# Revit family: EKF_EE_КорпусОднодверныйFORT_IP31_PROxima
name_source: partatom
category: Электрооборудование
units: mm (PartAtom-declared; Revit-internal decimal feet)

## family parameters
Всегда вертикально = Нет
На основе рабочей плоскости = Да
Общий = Да
При загрузке вырезать с полостями = Нет
Размер круглого соединителя = Использовать диаметр
Тип детали = Силовой щит
Точка расчета площади = Нет

## types (24) — shared parameters
ADSK_Единица измерения = шт.
ADSK_Завод-изготовитель = EKF
ADSK_Количество = 1
ADSK_Марка = Корпус FORT
ADSK_Материал = RAL 7035_Сталь
ADSK_Обозначение = Корпус FORT
D = 10 мм
Дверь_t = 21 мм
ЗадняяПанель_t = 24 мм
Изготовитель = EKF
КолОтв = 4
Крышка_t = 14 мм
Отступ = 20 мм
Серия номенклатуры = PROxima
Степень защиты IP = IP31
ТВ = EKF_2
Тип установки = Напольный
zero-valued in all types: ADSK_Масса, Отметка по умолчанию

## per-type parameters (varying)
| type | ADSK_Код изделия | ADSK_Размер_Высота | ADSK_Размер_Глубина | ADSK_Размер_Ширина | Каркас_h | Каркас_Глубина | Тип |
| Корпус FORT IP31 (1800x600x400) EKF PROxima | FK1864 | 1800 мм | 400 мм | 600 мм | 1786 мм | 350.5 мм | 177 мм |
| Корпус FORT IP31 (1800x600x600) EKF PROxima | FK1866 | 1800 мм | 600 мм | 600 мм | 1786 мм | 550.5 мм | 178 мм |
| Корпус FORT IP31 (1800x600x800) EKF PROxima | FK1868 | 1800 мм | 800 мм | 600 мм | 1786 мм | 750.5 мм | 179 мм |
| Корпус FORT IP31 (1800x800x400) EKF PROxima | FK1884 | 1800 мм | 400 мм | 800 мм | 1786 мм | 350.5 мм | 180 мм |
| Корпус FORT IP31 (1800x800x600) EKF PROxima | FK1886 | 1800 мм | 600 мм | 800 мм | 1786 мм | 550.5 мм | 181 мм |
| Корпус FORT IP31 (1800x800x800) EKF PROxima | FK1888 | 1800 мм | 800 мм | 800 мм | 1786 мм | 750.5 мм | 182 мм |
| Корпус FORT IP31 (2000x400x400) EKF PROxima | FK2044 | 2000 мм | 400 мм | 400 мм | 1986 мм | 350.5 мм | 186 мм |
| Корпус FORT IP31 (2000x400x600) EKF PROxima | FK2046 | 2000 мм | 600 мм | 400 мм | 1986 мм | 550.5 мм | 187 мм |
| Корпус FORT IP31 (2000x400x800) EKF PROxima | FK2048 | 2000 мм | 800 мм | 400 мм | 1986 мм | 750.5 мм | 188 мм |
| Корпус FORT IP31 (2000x600x400) EKF PROxima | FK2064 | 2000 мм | 400 мм | 600 мм | 1986 мм | 350.5 мм | 189 мм |
| Корпус FORT IP31 (2000x600x600) EKF PROxima | FK2066 | 2000 мм | 600 мм | 600 мм | 1986 мм | 550.5 мм | 190 мм |
| Корпус FORT IP31 (2000x600x800) EKF PROxima | FK2068 | 2000 мм | 800 мм | 600 мм | 1986 мм | 750.5 мм | 191 мм |
| Корпус FORT IP31 (2000x800x400) EKF PROxima | FK2084 | 2000 мм | 400 мм | 800 мм | 1986 мм | 350.5 мм | 192 мм |
| Корпус FORT IP31 (2000x800x600) EKF PROxima | FK2086 | 2000 мм | 600 мм | 800 мм | 1986 мм | 550.5 мм | 193 мм |
| Корпус FORT IP31 (2000x800x800) EKF PROxima | FK2088 | 2000 мм | 800 мм | 800 мм | 1986 мм | 750.5 мм | 194 мм |
| Корпус FORT IP31 (2200x400x400) EKF PROxima | FK2244 | 2200 мм | 400 мм | 400 мм | 2186 мм | 350.5 мм | 198 мм |
| Корпус FORT IP31 (2200x400x600) EKF PROxima | FK2246 | 2200 мм | 600 мм | 400 мм | 2186 мм | 550.5 мм | 199 мм |
| Корпус FORT IP31 (2200x400x800) EKF PROxima | FK2248 | 2200 мм | 800 мм | 400 мм | 2186 мм | 750.5 мм | 200 мм |
| Корпус FORT IP31 (2200x600x400) EKF PROxima | FK2264 | 2200 мм | 400 мм | 600 мм | 2186 мм | 350.5 мм | 201 мм |
| Корпус FORT IP31 (2200x600x600) EKF PROxima | FK2266 | 2200 мм | 600 мм | 600 мм | 2186 мм | 550.5 мм | 202 мм |
| Корпус FORT IP31 (2200x600x800) EKF PROxima | FK2268 | 2200 мм | 800 мм | 600 мм | 2186 мм | 750.5 мм | 203 мм |
| Корпус FORT IP31 (2200x800x400) EKF PROxima | FK2284 | 2200 мм | 400 мм | 800 мм | 2186 мм | 350.5 мм | 204 мм |
| Корпус FORT IP31 (2200x800x600) EKF PROxima | FK2286 | 2200 мм | 600 мм | 800 мм | 2186 мм | 550.5 мм | 205 мм |
| Корпус FORT IP31 (2200x800x800) EKF PROxima | FK2288 | 2200 мм | 800 мм | 800 мм | 2186 мм | 750.5 мм | 206 мм |

note: column(s) folded — value = type name in every type: ADSK_Наименование
